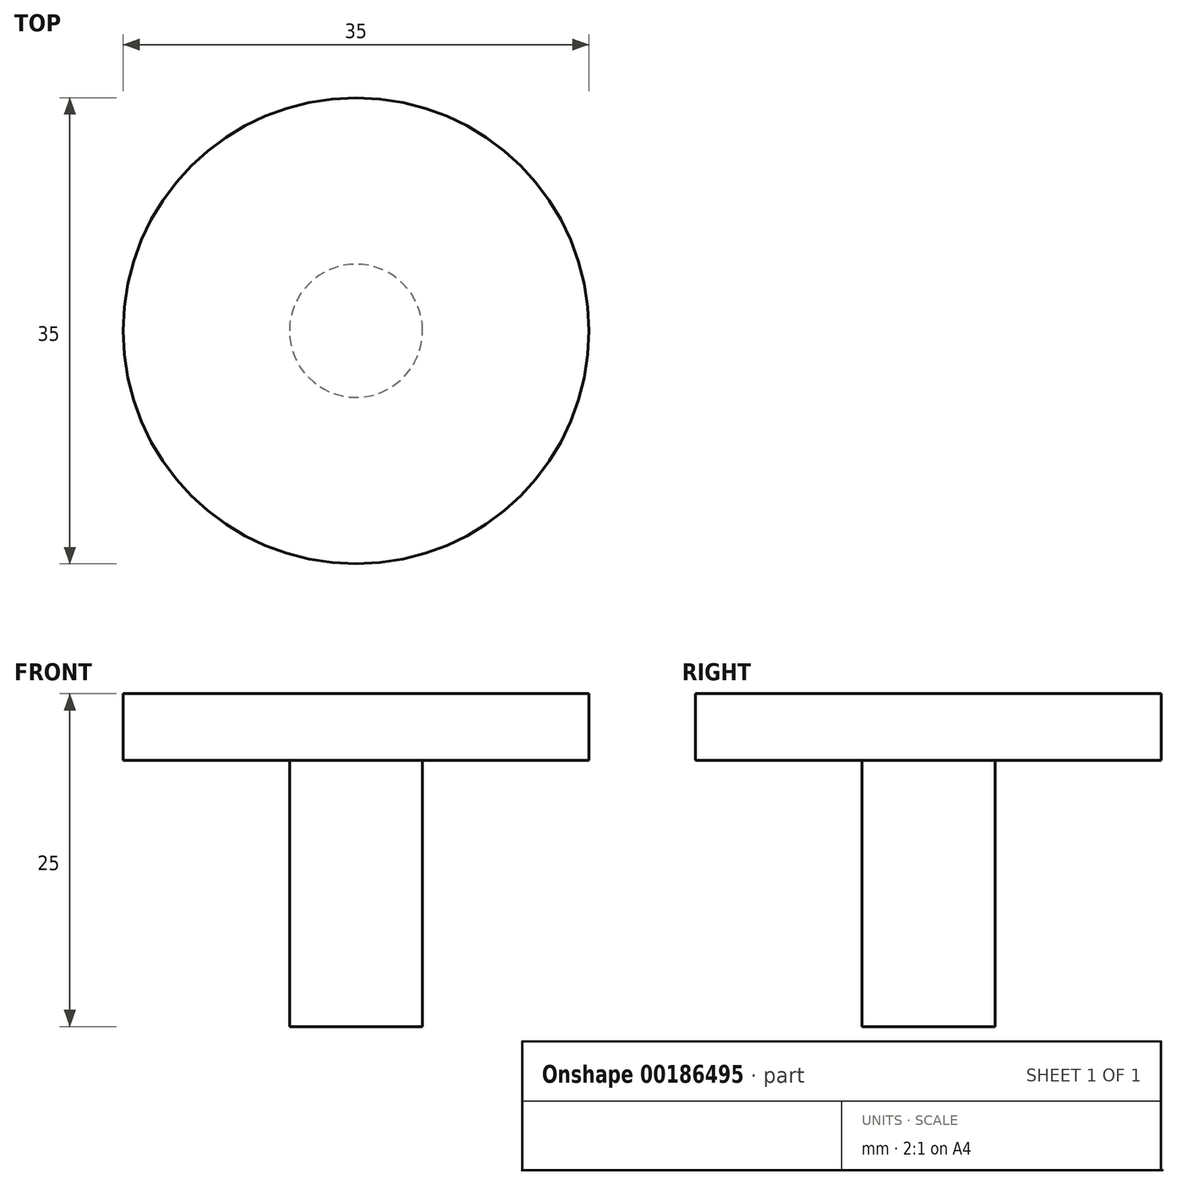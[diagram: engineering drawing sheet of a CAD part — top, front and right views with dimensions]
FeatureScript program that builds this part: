
annotation { "Feature Type Name" : "Feature", "Feature Type Description" : "" }
export const myFeature = defineFeature(function(context is Context, id is Id, definition is map)
    precondition{}
    {
        {
            var Q0;
            Q0=qCreatedBy(makeId("Front.planeOp"),FACE);
            var sketch = newSketch(context, id + "F0", { "sketchPlane" : qUnion([Q0])});
            skLineSegment(sketch, "E0", {"start": v(0, 25) * mm, "end": v(-17.5, 25) * mm});
            skLineSegment(sketch, "E1", {"start": v(-17.5, 25) * mm, "end": v(-17.5, 20) * mm});
            skLineSegment(sketch, "E2", {"start": v(-17.5, 20) * mm, "end": v(-5, 20) * mm});
            skLineSegment(sketch, "E3", {"start": v(-5, 20) * mm, "end": v(-5, 0) * mm});
            skLineSegment(sketch, "E4", {"start": v(-5, 0) * mm, "end": v(0, 0) * mm});
            skLineSegment(sketch, "E5", {"start": v(0, 0) * mm, "end": v(0, 25) * mm});
            skLineSegment(sketch, "E6", {"start": v(0, 36.87) * mm, "end": v(0, -17.42) * mm, "construction": true});
            skSolve(sketch);
        }
        {
            var Q0;
            Q0 = qSketchRegion(id + "F0", true);
            var Q1;
            Q1=sQuery(id+"F0.wireOp",EDGE,"E6");
            revolve(context, id + "F1", {"entities" : qUnion([Q0]), "axis" : qUnion([Q1]), "revolveType" : RevolveType.FULL});
        }
    });
